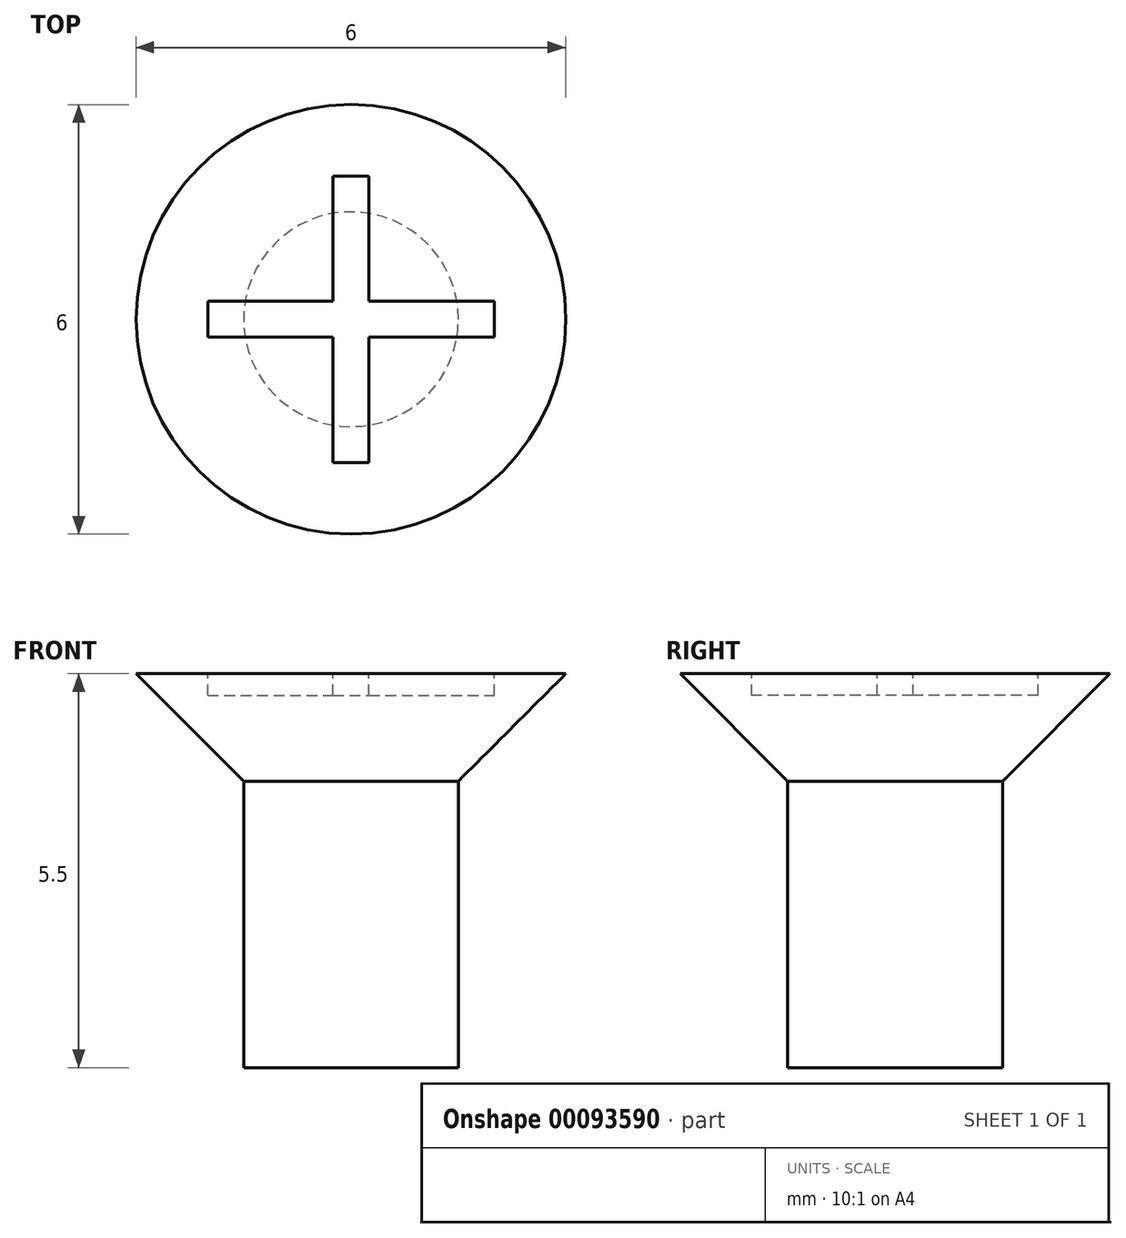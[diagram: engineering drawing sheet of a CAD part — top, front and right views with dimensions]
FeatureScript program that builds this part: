
annotation { "Feature Type Name" : "Feature", "Feature Type Description" : "" }
export const myFeature = defineFeature(function(context is Context, id is Id, definition is map)
    precondition{}
    {
        {
            var Q0;
            Q0=qCreatedBy(makeId("Top.planeOp"),FACE);
            var sketch = newSketch(context, id + "F0", { "sketchPlane" : qUnion([Q0])});
            skCircle(sketch, "E0", {"center": v(3.03, 7.58) * mm, "radius": 3 * mm});
            skSolve(sketch);
        }
        {
            var Q0;
            Q0=makeQuery(id+"F0.imprint","IMPRINT",FACE,{"disambiguationData":[TD([[makeQuery(id+"F0.imprint","IMPRINT",EDGE,{"derivedFrom":sQuery(id+"F0.wireOp",EDGE,"E0")}),1.0]])]});
            extrude(context, id + "F1", {"entities" : qUnion([Q0]), "depth" : 1.5 * mm});
        }
        {
            var Q0;
            Q0=makeQuery(id+"F1.opExtrude","CAP_EDGE",EDGE,{"disambiguationData":[OSD([sQuery(id+"F0.wireOp",EDGE,"E0")])],"isStart":true});
            chamfer(context, id + "F2", {"entities" : qUnion([Q0]), "width" : 1.5 * mm, "tangentPropagation" : true});
        }
        {
            var Q0;
            Q0=makeQuery(id+"F1.opExtrude","CAP_FACE",FACE,{"disambiguationData":[OSD([sQuery(id+"F0.wireOp",EDGE,"E0")])],"isStart":false});
            var sketch = newSketch(context, id + "F3", { "sketchPlane" : qUnion([Q0])});
            skLineSegment(sketch, "E1.bottom", {"start": v(2.78, 9.58) * mm, "end": v(3.28, 9.58) * mm});
            skLineSegment(sketch, "E1.top", {"start": v(3.03, 5.58) * mm, "end": v(3.28, 5.58) * mm});
            skLineSegment(sketch, "E1.left", {"start": v(2.78, 9.58) * mm, "end": v(2.78, 5.58) * mm});
            skLineSegment(sketch, "E1.right", {"start": v(3.28, 9.58) * mm, "end": v(3.28, 5.58) * mm});
            skPoint(sketch, "E2", {"position": v(3.03, 7.58) * mm});
            skPoint(sketch, "E2.positionSnap0", {"position": v(2.78, 7.58) * mm});
            skPoint(sketch, "E2.positionSnap1", {"position": v(3.03, 5.58) * mm});
            skLineSegment(sketch, "E3.bottom", {"start": v(1.03, 7.83) * mm, "end": v(5.03, 7.83) * mm});
            skLineSegment(sketch, "E3.top", {"start": v(1.03, 7.33) * mm, "end": v(5.03, 7.33) * mm});
            skLineSegment(sketch, "E3.left", {"start": v(1.03, 7.83) * mm, "end": v(1.03, 7.33) * mm});
            skLineSegment(sketch, "E3.right", {"start": v(5.03, 7.83) * mm, "end": v(5.03, 7.33) * mm});
            skPoint(sketch, "E4.positionSnap0", {"position": v(3.03, 7.83) * mm});
            skPoint(sketch, "E4.positionSnap1", {"position": v(1.03, 7.58) * mm});
            skLineSegment(sketch, "E5", {"start": v(3.03, 5.58) * mm, "end": v(2.78, 5.58) * mm});
            skSolve(sketch);
        }
        {
            var Q0;
            Q0 = qSketchRegion(id + "F3", true);
            extrude(context, id + "F4", {"entities" : qUnion([Q0]), "operationType" : NewBodyOperationType.REMOVE, "oppositeDirection" : true, "depth" : .3 * mm});
        }
        {
            var Q0;
            Q0=makeQuery(id+"F1.opExtrude","CAP_FACE",FACE,{"disambiguationData":[OSD([sQuery(id+"F0.wireOp",EDGE,"E0")])],"isStart":true});
            extrude(context, id + "F5", {"entities" : qUnion([Q0]), "operationType" : NewBodyOperationType.ADD, "depth" : 4 * mm});
        }
    });
